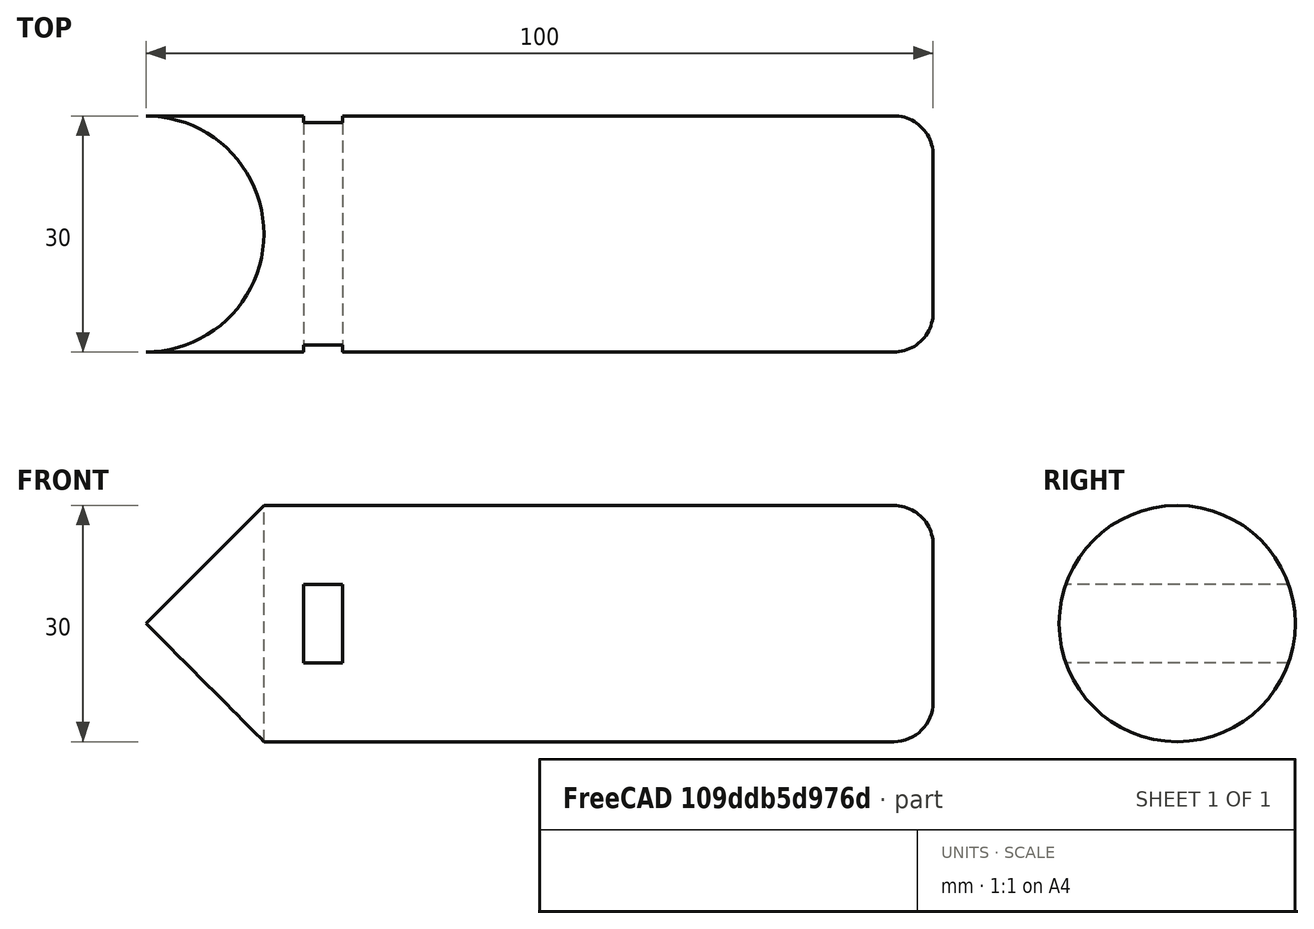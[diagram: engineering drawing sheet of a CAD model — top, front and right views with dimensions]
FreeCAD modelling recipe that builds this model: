
FCSTD DOCUMENT  (FreeCAD 0.16R)
Label: soporte antena
License: All rights reserved
LicenseURL: http://en.wikipedia.org/wiki/All_rights_reserved
objects: Part::Cylinder×2, Part::Cut×2, Part::Box×1, PartDesign::Fillet×1
note: 6 computed .brp shape members not serialized (recipe doc carries the construction recipe); baked Part::Feature solids carry a one-line shape summary decoded from their .brp

FEATURE [Part::Cylinder] Cylinder  label="Cilindro"
  Angle = 360
  Height = 100
  Placement = pos=(0,0,0) rot=(0,1,0;1.5708rad)
  Radius = 15
FEATURE [Part::Cylinder] Cylinder001  label="Cilindro001"
  Angle = 360
  Height = 100
  Placement = pos=(0,0,-44) rot=(0,0,1;0rad)
  Radius = 15
FEATURE [Part::Cut] Cut
  Base = -> Cylinder
  Tool = -> Cylinder001
FEATURE [Part::Box] Box  label="Cubo"
  Height = 48
  Length = 5
  Placement = pos=(20,27,-5) rot=(1,0,0;1.5708rad)
  Width = 10
FEATURE [Part::Cut] Cut001
  Base = -> Cut
  Tool = -> Box
FEATURE [PartDesign::Fillet] Fillet
  Base = -> Cut001 [Edge6]
  Radius = 5
